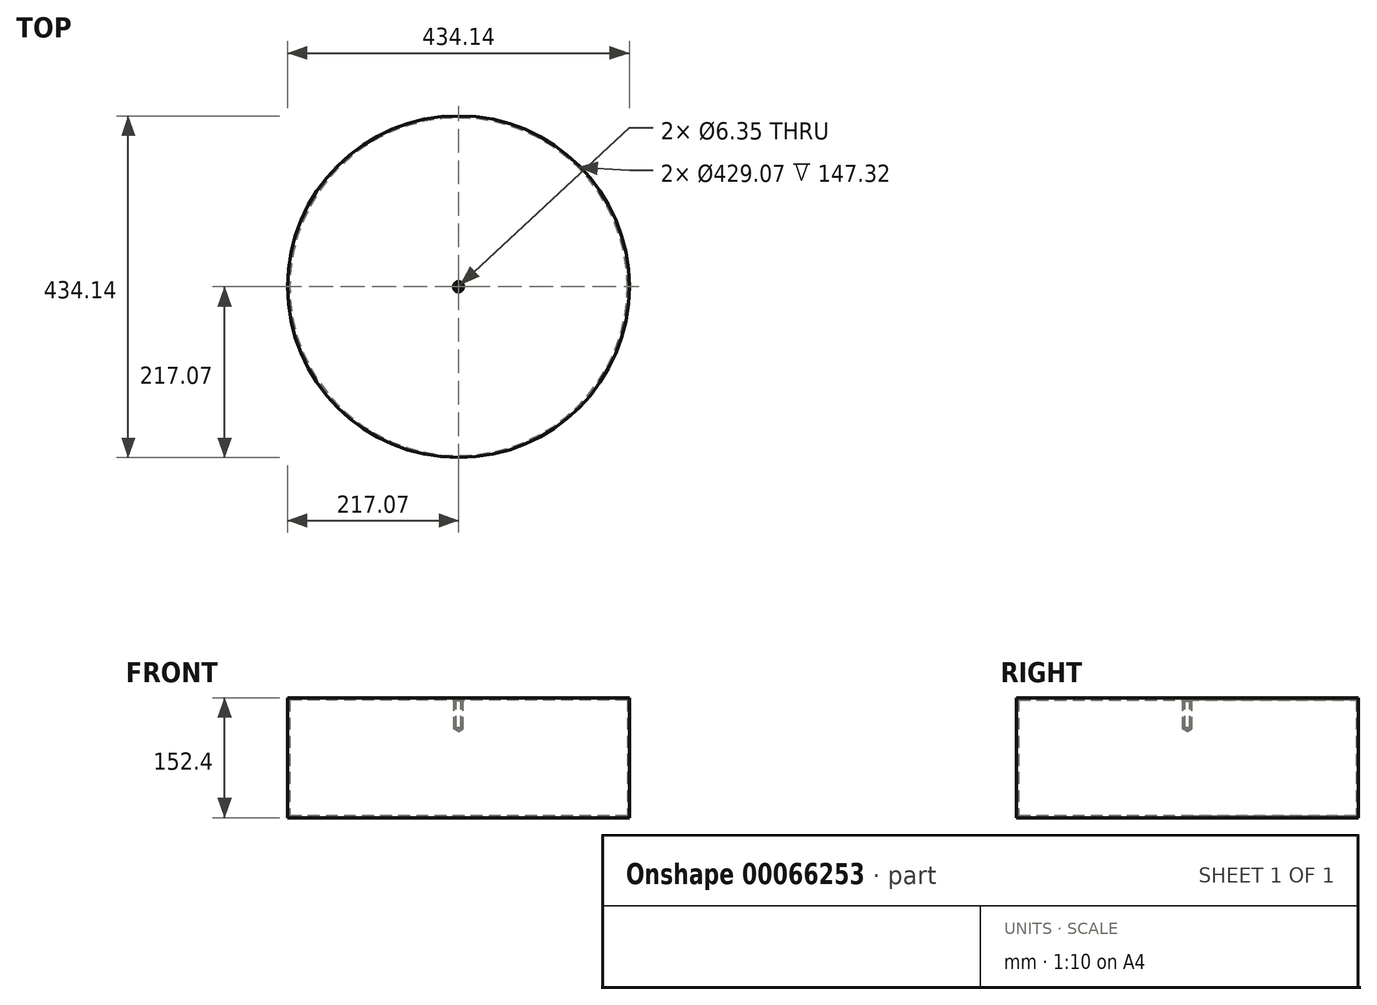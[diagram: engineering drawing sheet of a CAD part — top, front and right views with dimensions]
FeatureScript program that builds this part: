
annotation { "Feature Type Name" : "Feature", "Feature Type Description" : "" }
export const myFeature = defineFeature(function(context is Context, id is Id, definition is map)
    precondition{}
    {
        {
            var Q0;
            Q0=qCreatedBy(makeId("Top.planeOp"),FACE);
            var sketch = newSketch(context, id + "F0", { "sketchPlane" : qUnion([Q0])});
            skCircle(sketch, "E0", {"center": v(0, 0) * mm, "radius": 217.07 * mm});
            skSolve(sketch);
        }
        {
            var Q0;
            Q0=makeQuery(id+"F0.imprint","IMPRINT",FACE,{"disambiguationData":[TD([[makeQuery(id+"F0.imprint","IMPRINT",EDGE,{"derivedFrom":sQuery(id+"F0.wireOp",EDGE,"E0")}),1.0]])]});
            extrude(context, id + "F1", {"entities" : qUnion([Q0]), "depth" : 152.4 * mm});
        }
        {
            var Q0;
            Q0=makeQuery(id+"F1.opExtrude","CAP_FACE",FACE,{"disambiguationData":[OSD([sQuery(id+"F0.wireOp",EDGE,"E0")])],"isStart":false});
            var sketch = newSketch(context, id + "F2", { "sketchPlane" : qUnion([Q0])});
            skCircle(sketch, "E1", {"center": v(0, 0) * mm, "radius": 186.16 * mm});
            skSolve(sketch);
        }
        {
            var Q0;
            Q0=sQuery(id+"F2.wireOp",VERTEX,"E1.center");
            var Q1;
            Q1=makeQuery(id+"F1.opExtrude","SWEPT_BODY",BODY,{"disambiguationData":[OSD([sQuery(id+"F0.wireOp",EDGE,"E0")])]});
            hole(context, id + "F3", {"style" : HoleStyle.C_SINK, "holeDiameter" : 6.35 * mm, "cSinkDiameter" : 12.7 * mm, "endStyle" : HoleEndStyle.BLIND, "holeDepth" : 38.1 * mm, "locations" : qUnion([Q0]), "scope" : qUnion([Q1]), "cSinkAngle" : 90 * degree});
        }
        {
            var Q0;
            Q0=makeQuery(id+"F3.hole-0.boolean.opBoolean","COPY",FACE,{"derivedFrom":makeQuery(id+"F3.hole-0.opRevolve","SWEPT_FACE",FACE,{"disambiguationData":[OSD([sQuery(id+"F3.hole-0.sketch.wireOp",EDGE,"csink_start_line_1")])]})});
            var Q1;
            Q1=makeQuery(id+"F1.opExtrude","SWEPT_BODY",BODY,{"disambiguationData":[OSD([sQuery(id+"F0.wireOp",EDGE,"E0")])]});
            shell(context, id + "F4", {"isHollow" : true, "entities" : qUnion([Q0]), "parts" : qUnion([Q1]), "thickness" : 2.54 * mm});
        }
    });
